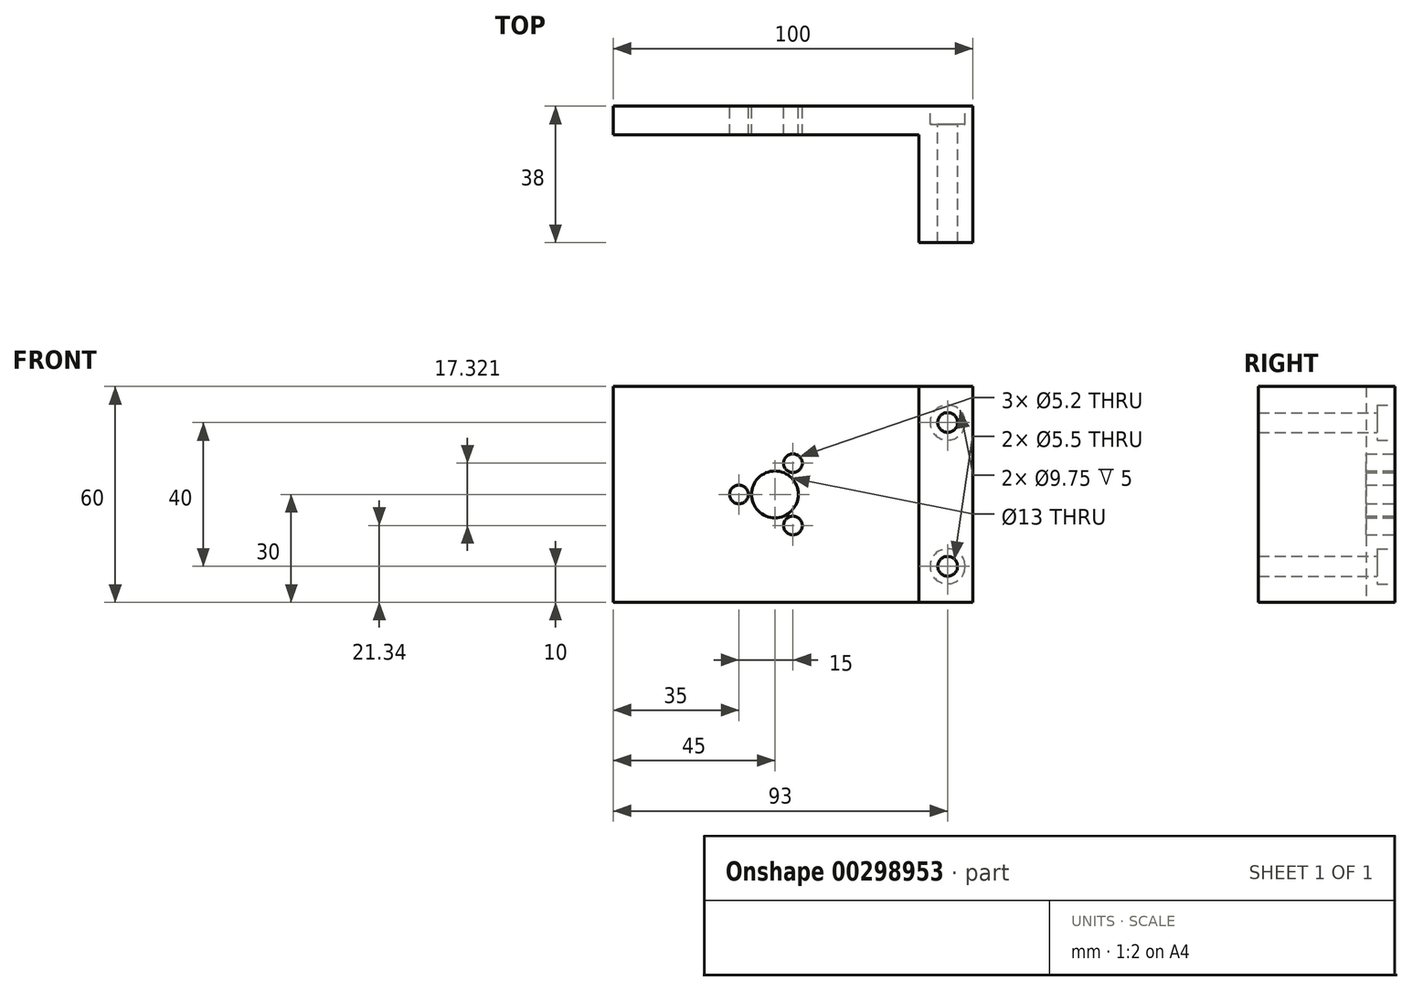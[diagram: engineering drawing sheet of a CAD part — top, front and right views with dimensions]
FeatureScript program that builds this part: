
annotation { "Feature Type Name" : "Feature", "Feature Type Description" : "" }
export const myFeature = defineFeature(function(context is Context, id is Id, definition is map)
    precondition{}
    {
        {
            var Q0;
            Q0=qCreatedBy(makeId("Front.planeOp"),FACE);
            var sketch = newSketch(context, id + "F0", { "sketchPlane" : qUnion([Q0])});
            skLineSegment(sketch, "E0.bottom", {"start": v(-50, 30) * mm, "end": v(50, 30) * mm});
            skLineSegment(sketch, "E0.top", {"start": v(-50, -30) * mm, "end": v(50, -30) * mm});
            skLineSegment(sketch, "E0.left", {"start": v(-50, 30) * mm, "end": v(-50, -30) * mm});
            skLineSegment(sketch, "E0.right", {"start": v(50, 30) * mm, "end": v(50, -30) * mm});
            skPoint(sketch, "E0.middle", {"position": v(0, 0) * mm});
            skPoint(sketch, "E1", {"position": v(43, 20) * mm});
            skPoint(sketch, "E2.MirrorP", {"position": v(43, -20) * mm});
            skPoint(sketch, "E3", {"position": v(-5, 0) * mm});
            skPoint(sketch, "E4", {"position": v(-15, 0) * mm});
            skLineSegment(sketch, "E5", {"start": v(-5, 0) * mm, "end": v(9.17, 24.54) * mm, "construction": true});
            skPoint(sketch, "E6", {"position": v(0, 8.66) * mm});
            skPoint(sketch, "E7.MirrorP", {"position": v(0, -8.66) * mm});
            skLineSegment(sketch, "E8.MirrorCS", {"start": v(-5, 0) * mm, "end": v(9.17, -24.54) * mm, "construction": true});
            skLineSegment(sketch, "E9.bottom", {"start": v(50, 30) * mm, "end": v(35, 30) * mm});
            skLineSegment(sketch, "E9.top", {"start": v(50, -30) * mm, "end": v(35, -30) * mm});
            skLineSegment(sketch, "E9.right", {"start": v(35, 30) * mm, "end": v(35, -30) * mm});
            skSolve(sketch);
        }
        {
            var Q0;
            Q0=makeQuery(id+"F0.imprint","IMPRINT",FACE,{"disambiguationData":[TD([[makeQuery(id+"F0.imprint","IMPRINT",EDGE,{"derivedFrom":sQuery(id+"F0.wireOp",EDGE,"E0.bottom")}),-1.0]])]});
            var Q1;
            Q1=makeQuery(id+"F0.imprint","IMPRINT",FACE,{"disambiguationData":[TD([[makeQuery(id+"F0.imprint","IMPRINT",EDGE,{"derivedFrom":sQuery(id+"F0.wireOp",EDGE,"E9.bottom")}),1.0]])]});
            extrude(context, id + "F1", {"entities" : qUnion([Q0, Q1]), "depth" : 8 * mm});
        }
        {
            var Q0;
            Q0=sQuery(id+"F0.wireOp",VERTEX,"E4");
            var Q1;
            Q1=sQuery(id+"F0.wireOp",VERTEX,"E7.MirrorP");
            var Q2;
            Q2=sQuery(id+"F0.wireOp",VERTEX,"E6");
            var Q3;
            Q3=makeQuery(id+"F1.opExtrude","SWEPT_BODY",BODY,{"disambiguationData":[OSD([sQuery(id+"F0.wireOp",EDGE,"E0.bottom"),sQuery(id+"F0.wireOp",EDGE,"E0.top"),sQuery(id+"F0.wireOp",EDGE,"E0.left"),sQuery(id+"F0.wireOp",EDGE,"E9.bottom"),sQuery(id+"F0.wireOp",EDGE,"E9.top"),sQuery(id+"F0.wireOp",EDGE,"E0.right")])]});
            hole(context, id + "F2", {"style" : HoleStyle.SIMPLE, "endStyle" : HoleEndStyle.THROUGH, "oppositeDirection" : true, "holeDiameter" : 5.2 * mm, "isTappedThrough" : true, "tappedDepth" : 12 * mm, "tapClearance" : 3, "locations" : qUnion([Q0, Q1, Q2]), "scope" : qUnion([Q3])});
        }
        {
            var Q0;
            Q0=sQuery(id+"F0.wireOp",VERTEX,"E3");
            var Q1;
            Q1=makeQuery(id+"F1.opExtrude","SWEPT_BODY",BODY,{"disambiguationData":[OSD([sQuery(id+"F0.wireOp",EDGE,"E0.bottom"),sQuery(id+"F0.wireOp",EDGE,"E0.top"),sQuery(id+"F0.wireOp",EDGE,"E0.left"),sQuery(id+"F0.wireOp",EDGE,"E9.bottom"),sQuery(id+"F0.wireOp",EDGE,"E9.top"),sQuery(id+"F0.wireOp",EDGE,"E0.right")])]});
            hole(context, id + "F3", {"style" : HoleStyle.SIMPLE, "endStyle" : HoleEndStyle.THROUGH, "oppositeDirection" : true, "holeDiameter" : 13 * mm, "isTappedThrough" : true, "tappedDepth" : 12 * mm, "tapClearance" : 3, "locations" : qUnion([Q0]), "scope" : qUnion([Q1])});
        }
        {
            var Q0;
            Q0=sQuery(id+"F0.wireOp",VERTEX,"E1");
            var Q1;
            Q1=sQuery(id+"F0.wireOp",VERTEX,"E2.MirrorP");
            var Q2;
            Q2=makeQuery(id+"F1.opExtrude","SWEPT_BODY",BODY,{"disambiguationData":[OSD([sQuery(id+"F0.wireOp",EDGE,"E0.bottom"),sQuery(id+"F0.wireOp",EDGE,"E0.top"),sQuery(id+"F0.wireOp",EDGE,"E0.left"),sQuery(id+"F0.wireOp",EDGE,"E9.bottom"),sQuery(id+"F0.wireOp",EDGE,"E9.top"),sQuery(id+"F0.wireOp",EDGE,"E0.right")])]});
            hole(context, id + "F4", {"style" : HoleStyle.C_BORE, "endStyle" : HoleEndStyle.THROUGH, "oppositeDirection" : true, "standardTappedOrClearance" : lookupTablePath({ "standard" : "ISO", "fit" : "Normal", "size" : "M5", "type" : "Clearance" }), "standardBlindInLast" : lookupTablePath({ "fit" : "Standard", "standard" : "ISO", "size" : "M5", "type" : "Clearance" }), "holeDiameter" : 5.5 * mm, "cBoreDiameter" : 9.75 * mm, "cBoreDepth" : 5 * mm, "isTappedThrough" : true, "tappedDepth" : 12 * mm, "tapClearance" : 3, "locations" : qUnion([Q0, Q1]), "scope" : qUnion([Q2])});
        }
        {
            var Q0;
            Q0=makeQuery(id+"F1.opExtrude","CAP_FACE",FACE,{"disambiguationData":[OSD([sQuery(id+"F0.wireOp",EDGE,"E0.bottom"),sQuery(id+"F0.wireOp",EDGE,"E0.top"),sQuery(id+"F0.wireOp",EDGE,"E0.left"),sQuery(id+"F0.wireOp",EDGE,"E9.bottom"),sQuery(id+"F0.wireOp",EDGE,"E9.top"),sQuery(id+"F0.wireOp",EDGE,"E0.right")])],"isStart":false});
            var sketch = newSketch(context, id + "F5", { "sketchPlane" : qUnion([Q0])});
            skLineSegment(sketch, "E10.bottom", {"start": v(50, 30) * mm, "end": v(35, 30) * mm});
            skLineSegment(sketch, "E10.top", {"start": v(50, -30) * mm, "end": v(35, -30) * mm});
            skLineSegment(sketch, "E10.left", {"start": v(50, 30) * mm, "end": v(50, -30) * mm});
            skLineSegment(sketch, "E10.right", {"start": v(35, 30) * mm, "end": v(35, -30) * mm});
            skSolve(sketch);
        }
        {
            var Q0;
            Q0=makeQuery(id+"F5.imprint","IMPRINT",FACE,{"disambiguationData":[TD([[makeQuery(id+"F5.imprint","IMPRINT",EDGE,{"derivedFrom":sQuery(id+"F5.wireOp",EDGE,"E10.bottom")}),-1.0]])]});
            extrude(context, id + "F6", {"entities" : qUnion([Q0]), "operationType" : NewBodyOperationType.ADD, "depth" : 30 * mm});
        }
    });
